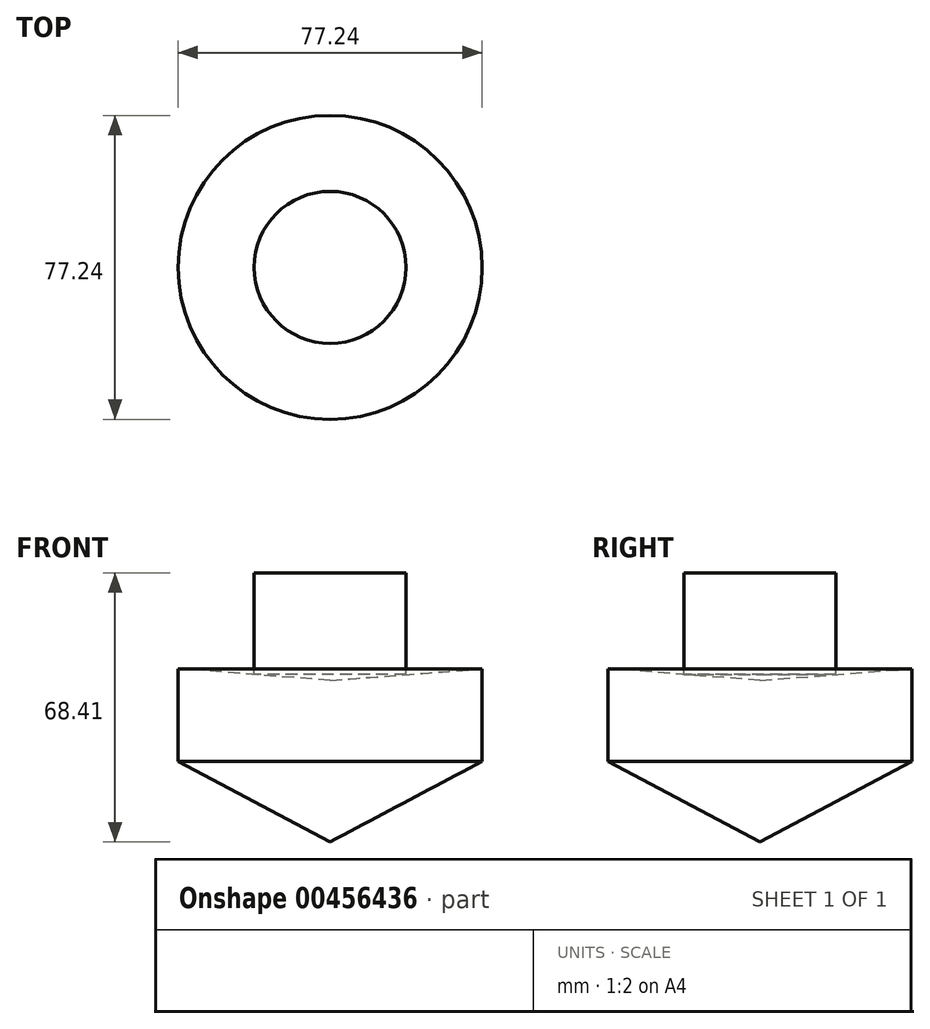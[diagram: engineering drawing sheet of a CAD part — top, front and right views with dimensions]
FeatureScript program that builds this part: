
annotation { "Feature Type Name" : "Feature", "Feature Type Description" : "" }
export const myFeature = defineFeature(function(context is Context, id is Id, definition is map)
    precondition{}
    {
        {
            var Q0;
            Q0=qCreatedBy(makeId("Front.planeOp"),FACE);
            var sketch = newSketch(context, id + "F0", { "sketchPlane" : qUnion([Q0])});
            skLineSegment(sketch, "E0", {"start": v(0, 41.1) * mm, "end": v(0, 0) * mm});
            skLineSegment(sketch, "E1", {"start": v(0, 0) * mm, "end": v(0, 0) * mm});
            skLineSegment(sketch, "E2", {"start": v(0, 41.1) * mm, "end": v(38.62, 20.55) * mm});
            skPoint(sketch, "E2.endSnap0", {"position": v(0, 20.55) * mm});
            skLineSegment(sketch, "E3", {"start": v(38.62, 20.55) * mm, "end": v(0, 0) * mm});
            skLineSegment(sketch, "E4", {"start": v(38.62, 44.06) * mm, "end": v(38.62, 20.55) * mm});
            skLineSegment(sketch, "E5", {"start": v(38.62, 44.06) * mm, "end": v(38.62, 44.06) * mm});
            skLineSegment(sketch, "E6", {"start": v(0, 41.1) * mm, "end": v(38.62, 44.06) * mm});
            skLineSegment(sketch, "E7.bottom", {"start": v(0, 68.4) * mm, "end": v(19.31, 68.4) * mm});
            skLineSegment(sketch, "E7.top", {"start": v(0, 42.58) * mm, "end": v(19.31, 42.58) * mm});
            skLineSegment(sketch, "E7.left", {"start": v(0, 68.4) * mm, "end": v(0, 42.58) * mm});
            skLineSegment(sketch, "E7.right", {"start": v(19.31, 68.4) * mm, "end": v(19.31, 42.58) * mm});
            skSolve(sketch);
        }
        {
            var Q0;
            Q0 = qSketchRegion(id + "F0", true);
            var Q1;
            Q1=sQuery(id+"F0.wireOp",EDGE,"E0");
            revolve(context, id + "F1", {"entities" : qUnion([Q0]), "axis" : qUnion([Q1]), "revolveType" : RevolveType.FULL});
        }
    });
